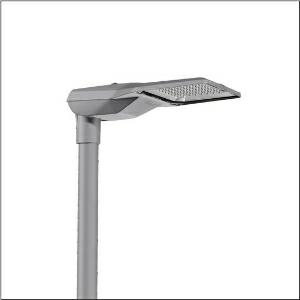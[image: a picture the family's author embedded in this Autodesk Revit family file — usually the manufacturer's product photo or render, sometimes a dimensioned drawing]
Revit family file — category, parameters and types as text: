
# Revit family: streetlight_sl_21_midi___p0_8a_5xe3u33s08nb_1026
name_source: partatom
category: Lighting Fixtures
units: mm (PartAtom-declared; Revit-internal decimal feet)

## family parameters
Cut with Voids When Loaded = No
Host = Face
Light Source = No
Part Type = Normal
Room Calculation Point = No
Round Connector Dimension = Use Diameter
Shared = No

## types (1)
- --- (1 x LED, 22900 lm, 151.2 W, 3000K)
    Apparent Load = 151 VA
    CIE Flux Codes = 36 69 97 100 100
    Color Rendering = 70
    Color Temperature = 3000K
    Default Elevation = 1800 mm
    Description = Streetlight SL 21 midi, mast luminaire, primary light control with lens, of PMMA, primary optical cover: cover, of toughened safety glass, transparent, light distribution: P0.8a, light emission: direct distribution, primary light characteristic: asymmetric, installation type: post-top, side-entry, LED, High Power LED, rated luminous flux: 22.900lm, luminous efficacy: 152lm/W, light colour: 730, colour temperature: 3000K, control gear: D4i, control: pre-setting: logarithmic dimming characteristic, flexible luminous flux parameterisation, time-dependent luminous flux control, constant luminous flux control, overheat protection, mains connection: 230..240V, AC, 50/60Hz, start of lifetime: 151W, end of service life: 157W, reduction: 70W, luminaire housing, of diecast aluminium, powder-coated, SITECO metallic grey (DB 702S), corrosivity category C5 high according to DIN EN ISO 12944, multi-level sealing system, sealing non-destructively replaceable, inclination adjustable: 0°, 5°, 10°, 15°, please order mast flange separately, length: 644mm, width: 335mm, height: 110mm, mast flange for spigot size: 42mm (side-entry): 5XC10008XM4, 60/48mm (side-entry/post-top): 5XC10108XM2, 76/60mm (side-entry/post-top): 5XC10108XM1, mounting height: 4..8m, Smart Interface above, protection rating (complete): IP66, insulation class (complete): insulation class II (safety insulation), certification: CE, ENEC, ENEC+, VDE, impact resistance: IK10, permissible operating ambient temperature for outdoor applications: -40..+50°C, standard-compliant lighting for roads and squares, packaging unit: 1 piece

Light Distribution: P0.8a
    Height = 111 mm
    Lamp = 1 x LED
    Lamp Light Flux = 22900 lm
    Lamp Power = 151.2 W
    Lamp count = 1
    Length = 644 mm
    Luminous efficacy = 151 lm/W
    Manufacturer = Siteco
    ModVariant = No
    Model = 5XE3U33S08NB
    Number of Poles = 1
    OnlyDefault = Yes
    Power Factor = 1
    Product Name = Streetlight SL 21 midi | P0.8a
    Product group = mast luminaire | pylon top
    ProductGroupID = 6100
    Protection Class = Protection class II
    Protection Degree = IP 66
    RLX_Detail_Level = 1
    RLX_Emergency_Light_Flux = 0 lm
    RLX_Emergency_Type = 0
    RLX_Emergency_Type_DB = No
    RlxData = <blob elided: 90865 chars, md5=16d903dc>
    Socket = socket
    Standby Power = 0 W
    System Light Flux = 22901 lm
    System Power = 151 W
    Type Comments = factory setting: luminous flux: 100 % | dim-lin: 254 | 802 mA
    Type Image = l_1004302.jpg
    URL = http://relux.com
    VarID = @adj_079181
    Voltage = 0 V
    Weight = 0.00 kg
    Width = 336 mm

## geometry (parser evidence)
native form markers: Blend x4, Sweep x10
no freeform markers — native parametric forms only
